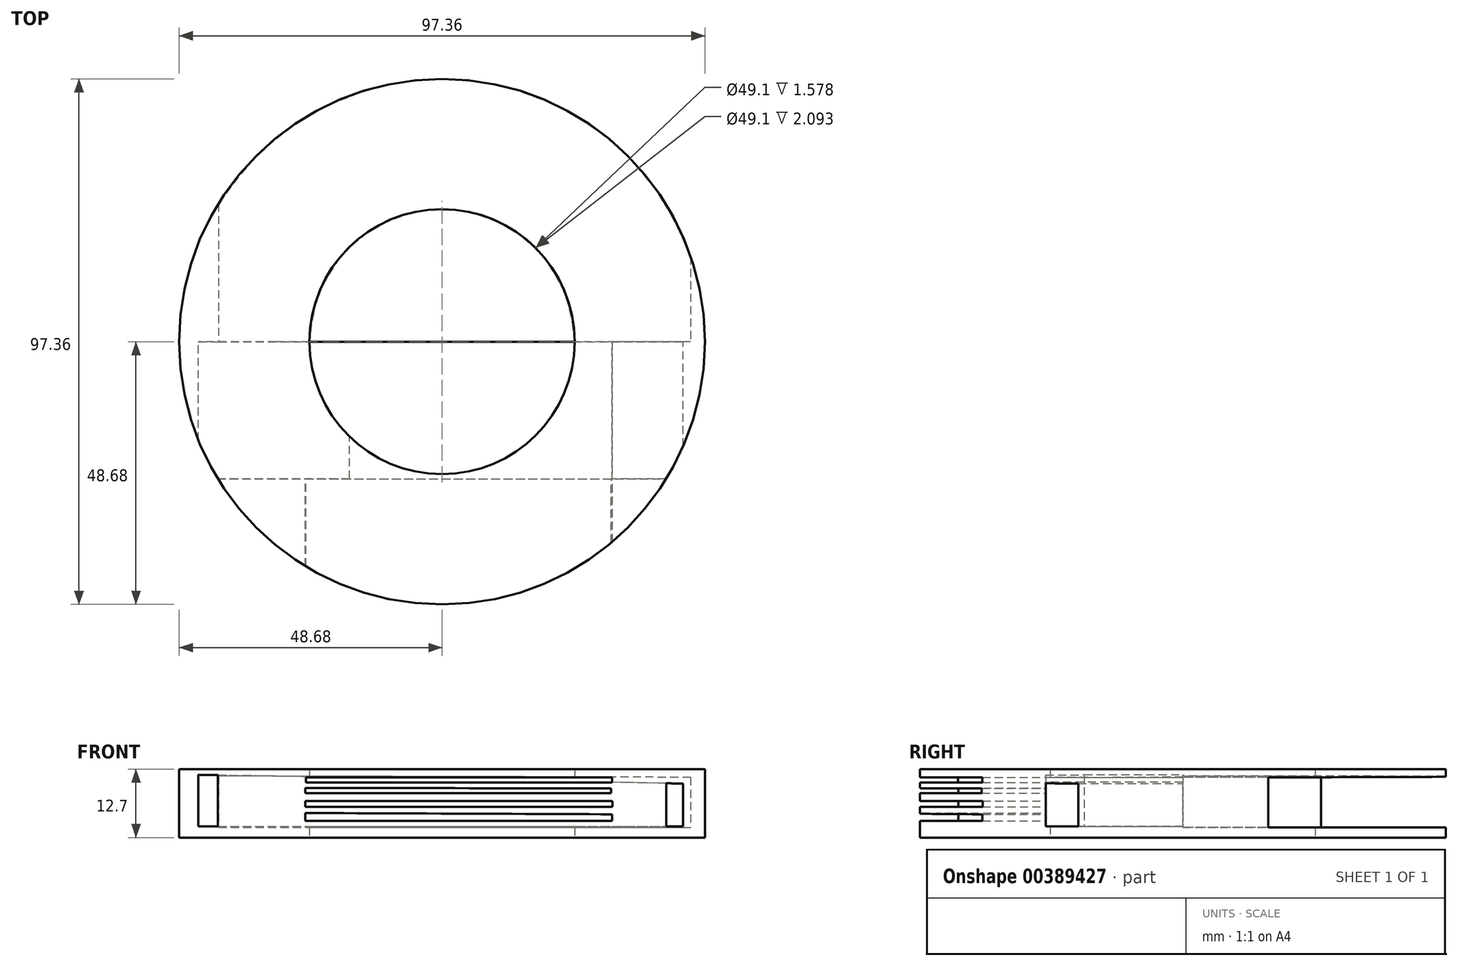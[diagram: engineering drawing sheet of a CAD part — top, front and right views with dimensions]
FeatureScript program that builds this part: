
annotation { "Feature Type Name" : "Feature", "Feature Type Description" : "" }
export const myFeature = defineFeature(function(context is Context, id is Id, definition is map)
    precondition{}
    {
        {
            var Q0;
            Q0=qCreatedBy(makeId("Top.planeOp"),FACE);
            var sketch = newSketch(context, id + "F0", { "sketchPlane" : qUnion([Q0])});
            skCircle(sketch, "E0", {"center": v(0, 0) * mm, "radius": 48.68 * mm});
            skCircle(sketch, "E1", {"center": v(0, 0) * mm, "radius": 24.55 * mm});
            skSolve(sketch);
        }
        {
            var Q0;
            Q0=makeQuery(id+"F0.imprint","IMPRINT",FACE,{"disambiguationData":[TD([[makeQuery(id+"F0.imprint","IMPRINT",EDGE,{"derivedFrom":sQuery(id+"F0.wireOp",EDGE,"E0")}),1.0]])]});
            extrude(context, id + "F1", {"entities" : qUnion([Q0]), "depth" : 12.7 * mm});
        }
        {
            var Q0;
            Q0=makeQuery(id+"F0.imprint","IMPRINT",FACE,{"disambiguationData":[TD([[makeQuery(id+"F0.imprint","IMPRINT",EDGE,{"derivedFrom":sQuery(id+"F0.wireOp",EDGE,"E1")}),1.0]])]});
            extrude(context, id + "F2", {"entities" : qUnion([Q0]), "depth" : 5.08 * mm});
        }
        {
            var Q0;
            Q0=qCreatedBy(makeId("Front.planeOp"),FACE);
            var sketch = newSketch(context, id + "F3", { "sketchPlane" : qUnion([Q0])});
            skLineSegment(sketch, "E2", {"start": v(-41.4, 11.4) * mm, "end": v(-41.4, 1.86) * mm});
            skLineSegment(sketch, "E3", {"start": v(-41.4, 1.86) * mm, "end": v(46.05, 1.86) * mm});
            skLineSegment(sketch, "E4", {"start": v(46.05, 1.86) * mm, "end": v(46.05, 11.16) * mm});
            skLineSegment(sketch, "E5", {"start": v(46.05, 11.16) * mm, "end": v(-41.4, 11.4) * mm});
            skSolve(sketch);
        }
        {
            var Q0;
            Q0 = qSketchRegion(id + "F3", true);
            extrude(context, id + "F4", {"entities" : qUnion([Q0]), "operationType" : NewBodyOperationType.REMOVE, "oppositeDirection" : true, "depth" : 50.8 * mm});
        }
        {
            var Q0;
            Q0=qCreatedBy(makeId("Front.planeOp"),FACE);
            var sketch = newSketch(context, id + "F5", { "sketchPlane" : qUnion([Q0])});
            skLineSegment(sketch, "E6", {"start": v(-45.12, 11.63) * mm, "end": v(-45.12, 2.1) * mm});
            skLineSegment(sketch, "E7", {"start": v(-45.12, 2.1) * mm, "end": v(44.66, 2.1) * mm});
            skLineSegment(sketch, "E8", {"start": v(44.66, 2.1) * mm, "end": v(44.66, 10) * mm});
            skLineSegment(sketch, "E9", {"start": v(44.66, 10) * mm, "end": v(-45.12, 11.63) * mm});
            skSolve(sketch);
        }
        {
            var Q0;
            Q0 = qSketchRegion(id + "F5", true);
            extrude(context, id + "F6", {"entities" : qUnion([Q0]), "operationType" : NewBodyOperationType.REMOVE, "depth" : 25.4 * mm});
        }
        {
            var Q0;
            Q0=qCreatedBy(makeId("Front.planeOp"),FACE);
            var sketch = newSketch(context, id + "F7", { "sketchPlane" : qUnion([Q0])});
            skLineSegment(sketch, "E10", {"start": v(-25.23, 11.12) * mm, "end": v(31.47, 11.12) * mm});
            skLineSegment(sketch, "E11", {"start": v(31.47, 11.12) * mm, "end": v(31.47, 10.22) * mm});
            skLineSegment(sketch, "E12", {"start": v(31.47, 10.22) * mm, "end": v(-25.23, 10.22) * mm});
            skLineSegment(sketch, "E13", {"start": v(-25.23, 10.22) * mm, "end": v(-25.23, 11.12) * mm});
            skLineSegment(sketch, "E14", {"start": v(-25.3, 9.19) * mm, "end": v(-25.3, 8.22) * mm});
            skLineSegment(sketch, "E15", {"start": v(-25.3, 8.22) * mm, "end": v(31.33, 8.22) * mm});
            skLineSegment(sketch, "E16", {"start": v(31.33, 8.22) * mm, "end": v(31.33, 9.12) * mm});
            skLineSegment(sketch, "E17", {"start": v(31.33, 9.12) * mm, "end": v(-25.3, 9.19) * mm});
            skLineSegment(sketch, "E18", {"start": v(-25.3, 6.77) * mm, "end": v(-25.3, 5.66) * mm});
            skLineSegment(sketch, "E19", {"start": v(-25.3, 5.66) * mm, "end": v(31.54, 5.66) * mm});
            skLineSegment(sketch, "E20", {"start": v(31.54, 5.66) * mm, "end": v(31.54, 6.77) * mm});
            skLineSegment(sketch, "E21", {"start": v(31.54, 6.77) * mm, "end": v(-25.3, 6.77) * mm});
            skLineSegment(sketch, "E22", {"start": v(-25.3, 4.55) * mm, "end": v(-25.3, 3.1) * mm});
            skLineSegment(sketch, "E23", {"start": v(-25.3, 3.1) * mm, "end": v(31.49, 3.1) * mm});
            skLineSegment(sketch, "E24", {"start": v(31.49, 3.1) * mm, "end": v(31.49, 4.31) * mm});
            skLineSegment(sketch, "E25", {"start": v(31.49, 4.31) * mm, "end": v(-25.3, 4.55) * mm});
            skSolve(sketch);
        }
        {
            var Q0;
            Q0 = qSketchRegion(id + "F7", true);
            extrude(context, id + "F8", {"entities" : qUnion([Q0]), "operationType" : NewBodyOperationType.REMOVE, "depth" : 127 * mm});
        }
    });
